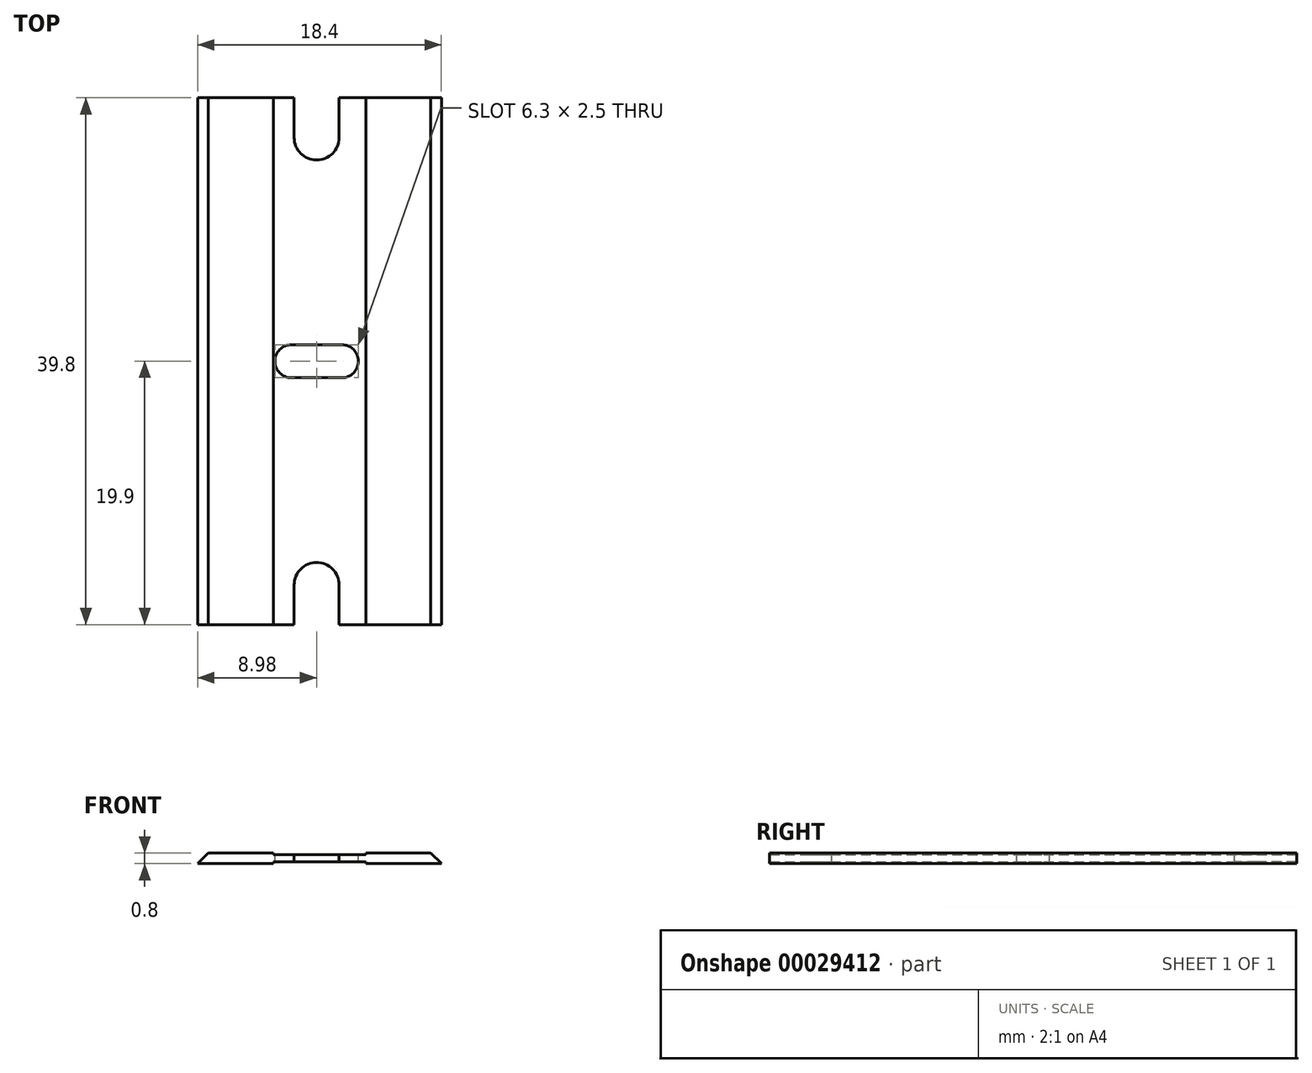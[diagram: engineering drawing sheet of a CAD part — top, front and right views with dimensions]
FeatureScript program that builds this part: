
annotation { "Feature Type Name" : "Feature", "Feature Type Description" : "" }
export const myFeature = defineFeature(function(context is Context, id is Id, definition is map)
    precondition{}
    {
        {
            var Q0;
            Q0=qCreatedBy(makeId("Top.planeOp"),FACE);
            var sketch = newSketch(context, id + "F0", { "sketchPlane" : qUnion([Q0])});
            skLineSegment(sketch, "E0.rect.bottom", {"start": v(-8.98, 19.9) * mm, "end": v(9.42, 19.9) * mm});
            skLineSegment(sketch, "E0.rect.top", {"start": v(-8.98, -19.9) * mm, "end": v(9.42, -19.9) * mm});
            skLineSegment(sketch, "E0.rect.left", {"start": v(-8.98, 19.9) * mm, "end": v(-8.98, -19.9) * mm});
            skLineSegment(sketch, "E0.rect.right", {"start": v(9.42, 19.9) * mm, "end": v(9.42, -19.9) * mm});
            skPoint(sketch, "E0.rect.middle", {"position": v(0.22, 0) * mm});
            skSolve(sketch);
        }
        {
            var Q0;
            Q0=makeQuery(id+"F0.imprint","IMPRINT",FACE,{"disambiguationData":[TD([[makeQuery(id+"F0.imprint","IMPRINT",EDGE,{"derivedFrom":sQuery(id+"F0.wireOp",EDGE,"E0.rect.bottom")}),-1.0]])]});
            extrude(context, id + "F1", {"entities" : qUnion([Q0]), "endBound" : BoundingType.SYMMETRIC, "depth" : 0.55 * mm});
        }
        {
            var Q0;
            Q0=makeQuery(id+"F1.opExtrude","CAP_FACE",FACE,{"disambiguationData":[OSD([sQuery(id+"F0.wireOp",EDGE,"E0.rect.bottom"),sQuery(id+"F0.wireOp",EDGE,"E0.rect.top"),sQuery(id+"F0.wireOp",EDGE,"E0.rect.left"),sQuery(id+"F0.wireOp",EDGE,"E0.rect.right")])],"isStart":false});
            var Q1;
            Q1=makeQuery(id+"F1.opExtrude","CAP_FACE",FACE,{"disambiguationData":[OSD([sQuery(id+"F0.wireOp",EDGE,"E0.rect.bottom"),sQuery(id+"F0.wireOp",EDGE,"E0.rect.top"),sQuery(id+"F0.wireOp",EDGE,"E0.rect.left"),sQuery(id+"F0.wireOp",EDGE,"E0.rect.right")])],"isStart":true});
            cPlane(context, id + "F2", {"entities" : qUnion([Q0, Q1]), "cplaneType" : CPlaneType.MID_PLANE, "offset" : 150 * mm, "width" : 150 * mm, "height" : 150 * mm});
        }
        {
            var Q0;
            Q0=qCreatedBy(id+"F2.planeOp",FACE);
            var sketch = newSketch(context, id + "F3", { "sketchPlane" : qUnion([Q0])});
            skLineSegment(sketch, "E1.0.1", {"start": v(9.42, 19.9) * mm, "end": v(9.42, -19.9) * mm});
            skLineSegment(sketch, "E1.0.2", {"start": v(9.42, -19.9) * mm, "end": v(3.72, -19.9) * mm});
            skLineSegment(sketch, "E1.0.3", {"start": v(-8.98, -19.9) * mm, "end": v(-8.98, 19.9) * mm});
            skLineSegment(sketch, "E2", {"start": v(-8.98, 19.9) * mm, "end": v(-3.28, 19.9) * mm});
            skLineSegment(sketch, "E3", {"start": v(9.42, 19.9) * mm, "end": v(3.72, 19.9) * mm});
            skLineSegment(sketch, "E4", {"start": v(-3.28, 19.9) * mm, "end": v(-3.28, -19.9) * mm});
            skLineSegment(sketch, "E5", {"start": v(3.72, 19.9) * mm, "end": v(3.72, -19.9) * mm});
            skLineSegment(sketch, "E6.trimOffspring", {"start": v(-3.28, -19.9) * mm, "end": v(-8.98, -19.9) * mm});
            skSolve(sketch);
        }
        {
            var Q0;
            Q0 = qSketchRegion(id + "F3", true);
            extrude(context, id + "F4", {"entities" : qUnion([Q0]), "operationType" : NewBodyOperationType.ADD, "endBound" : BoundingType.SYMMETRIC, "depth" : 0.8 * mm});
        }
        {
            var Q0;
            Q0=makeQuery(id+"F4.opExtrude","CAP_EDGE",EDGE,{"disambiguationData":[OSD([sQuery(id+"F3.wireOp",EDGE,"E1.0.1")])],"isStart":false});
            chamfer(context, id + "F5", {"entities" : qUnion([Q0]), "chamferType" : ChamferType.OFFSET_ANGLE, "width" : 0.8 * mm, "oppositeDirection" : false, "angle" : 45 * degree, "tangentPropagation" : true});
        }
        {
            var Q0;
            Q0=makeQuery(id+"F4.opExtrude","CAP_EDGE",EDGE,{"disambiguationData":[OSD([sQuery(id+"F3.wireOp",EDGE,"E1.0.3")])],"isStart":false});
            chamfer(context, id + "F6", {"entities" : qUnion([Q0]), "chamferType" : ChamferType.OFFSET_ANGLE, "width" : 0.8 * mm, "oppositeDirection" : false, "angle" : 45 * degree, "tangentPropagation" : true});
        }
        {
            var Q0;
            Q0=qCreatedBy(id+"F2.planeOp",FACE);
            var sketch = newSketch(context, id + "F7", { "sketchPlane" : qUnion([Q0])});
            skLineSegment(sketch, "E7", {"start": v(1.7, -19.9) * mm, "end": v(1.7, -16.9) * mm});
            skLineSegment(sketch, "E8.MirrorCS", {"start": v(-1.7, -19.9) * mm, "end": v(-1.7, -16.9) * mm});
            skArc(sketch, "E9", {"start": v(1.7, -16.9) * mm, "mid": v(0, -15.2) * mm, "end": v(-1.7, -16.9) * mm});
            skLineSegment(sketch, "E10.MirrorCS", {"start": v(1.7, 19.9) * mm, "end": v(1.7, 16.9) * mm});
            skArc(sketch, "E11.MirrorCS", {"start": v(1.7, 16.9) * mm, "mid": v(0, 15.2) * mm, "end": v(-1.7, 16.9) * mm});
            skLineSegment(sketch, "E12.MirrorCS", {"start": v(-1.7, 19.9) * mm, "end": v(-1.7, 16.9) * mm});
            skLineSegment(sketch, "E13", {"start": v(0, 1.25) * mm, "end": v(-1.9, 1.25) * mm});
            skLineSegment(sketch, "E14", {"start": v(0, -1.25) * mm, "end": v(-1.9, -1.25) * mm});
            skArc(sketch, "E15", {"start": v(-1.9, 1.25) * mm, "mid": v(-3.15, 0) * mm, "end": v(-1.9, -1.25) * mm});
            skLineSegment(sketch, "E16.MirrorCS", {"start": v(0, -1.25) * mm, "end": v(1.9, -1.25) * mm});
            skArc(sketch, "E17.MirrorCS", {"start": v(1.9, 1.25) * mm, "mid": v(3.15, 0) * mm, "end": v(1.9, -1.25) * mm});
            skLineSegment(sketch, "E18.MirrorCS", {"start": v(0, 1.25) * mm, "end": v(1.9, 1.25) * mm});
            skLineSegment(sketch, "E19", {"start": v(1.7, -19.9) * mm, "end": v(-1.7, -19.9) * mm});
            skLineSegment(sketch, "E20", {"start": v(1.7, 19.9) * mm, "end": v(-1.7, 19.9) * mm});
            skSolve(sketch);
        }
        {
            var Q0;
            Q0 = qSketchRegion(id + "F7", true);
            extrude(context, id + "F8", {"entities" : qUnion([Q0]), "operationType" : NewBodyOperationType.REMOVE, "endBound" : BoundingType.SYMMETRIC, "oppositeDirection" : true, "depth" : 25 * mm});
        }
    });
